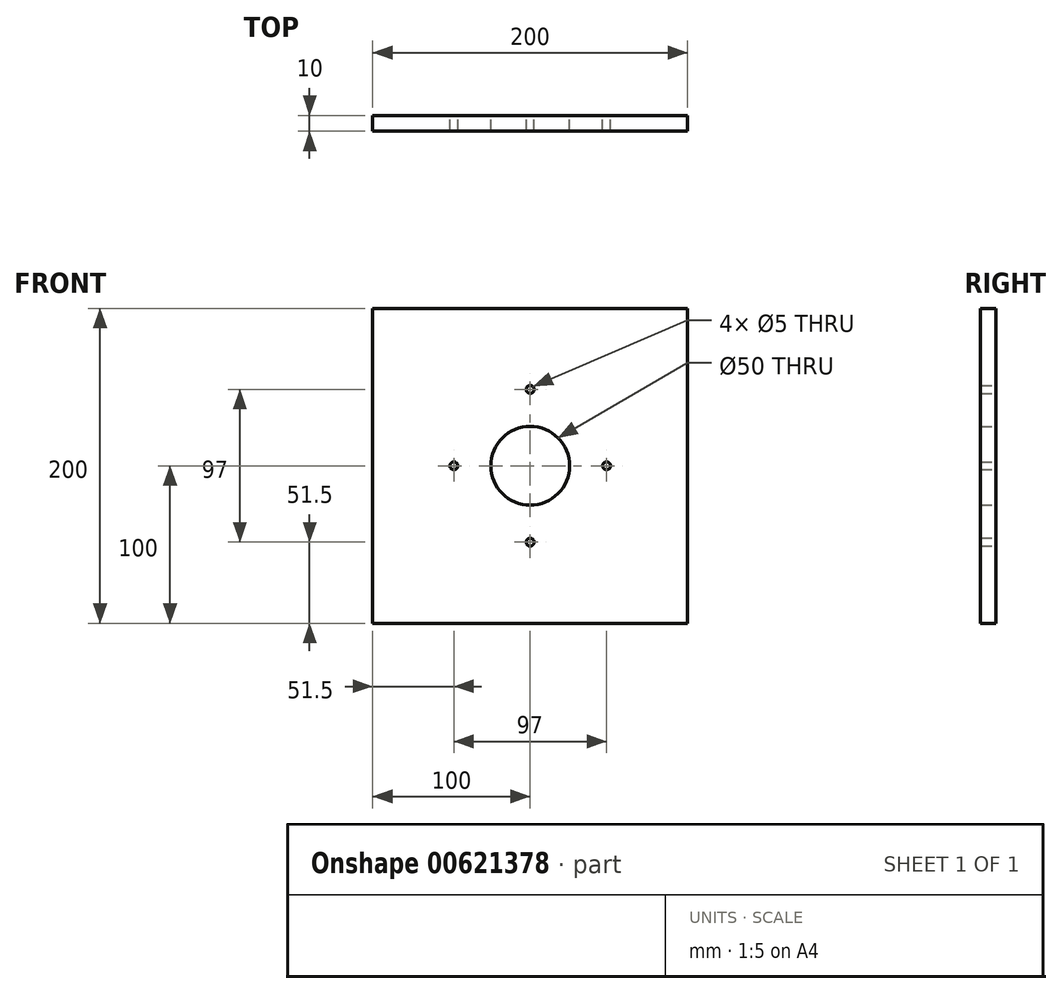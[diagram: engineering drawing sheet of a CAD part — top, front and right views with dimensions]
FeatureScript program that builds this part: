
annotation { "Feature Type Name" : "Feature", "Feature Type Description" : "" }
export const myFeature = defineFeature(function(context is Context, id is Id, definition is map)
    precondition{}
    {
        {
            var Q0;
            Q0=qCreatedBy(makeId("Front.planeOp"),FACE);
            var sketch = newSketch(context, id + "F0", { "sketchPlane" : qUnion([Q0])});
            skCircle(sketch, "E0", {"center": v(0, 0) * mm, "radius": 25 * mm});
            skCircle(sketch, "E1", {"center": v(0, 0) * mm, "radius": 48.5 * mm, "construction": true});
            skLineSegment(sketch, "E2.bottom", {"start": v(100, -100) * mm, "end": v(-100, -100) * mm});
            skLineSegment(sketch, "E2.top", {"start": v(100, 100) * mm, "end": v(-100, 100) * mm});
            skLineSegment(sketch, "E2.left", {"start": v(100, -100) * mm, "end": v(100, 100) * mm});
            skLineSegment(sketch, "E2.right", {"start": v(-100, -100) * mm, "end": v(-100, 100) * mm});
            skCircle(sketch, "E3", {"center": v(0, 48.5) * mm, "radius": 2.5 * mm});
            skCircle(sketch, "E4", {"center": v(48.5, 0) * mm, "radius": 2.5 * mm});
            skCircle(sketch, "E5", {"center": v(0, -48.5) * mm, "radius": 2.5 * mm});
            skCircle(sketch, "E6", {"center": v(-48.5, 0) * mm, "radius": 2.5 * mm});
            skSolve(sketch);
        }
        {
            var Q0;
            Q0 = qSketchRegion(id + "F0", true);
            extrude(context, id + "F1", {"entities" : qUnion([Q0]), "depth" : 10 * mm, "offsetDistance" : 25 * mm});
        }
    });
